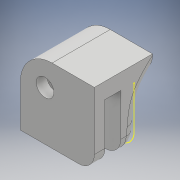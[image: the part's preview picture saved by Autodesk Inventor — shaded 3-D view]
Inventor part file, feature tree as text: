
AUTODESK INVENTOR PART (.ipt)
format: ipt  version: 2017 (Build 210142000, 142)  size: 299,520 bytes
history: native  units: mm
features: sketch x5, extrude x4, other x2, plane x1, loft x1, fillet x1, projected_geometry x1
ambient origin geometry x8: Origin, YZ Plane, XZ Plane, XY Plane, X Axis, Y Axis, Z Axis, Center Point
bodies: Solid1 (feature_tree)
feature tree (15):
  extrude  "Extrusion1"  Depth=3.0mm
  extrude  "Extrusion2"  Depth=3.0mm
  plane  "Work Plane1"
  extrude  "Extrusion3"  Depth=11.0mm TaperAngle=0.0deg
  sketch  "Sketch4"  dims[d7=2.0mm d8=0.0mm d9=3.0mm d10=2.5mm d11=0.0mm]
  loft  "Loft2"
  fillet  "Fillet1"  Radius=2.5mm
  extrude  "Extrusion4"  TaperAngle=0.0deg  [1 undecoded]
  sketch  "Sketch1"  dims[d0=3.0mm d1=3.0mm]
  sketch  "Sketch2"  dims[d2=8.0mm d3=3.0mm]
  sketch  "Sketch3"  dims[d4=8.0mm d5=11.0mm d6=0.0mm]
  projected_geometry  "Projected Loop1"
  other  "Edges3"
  other  "Edges4"
  sketch  "Sketch5"  dims[d16=0.0mm d17=90.0deg d18=0.0mm d19=90.0deg d20=2.0mm d21=3.333333mm d22=3.0mm d23=3.0mm d24=2.5mm d25=0.0mm]
note: 1 required parameter value undecoded (feature->parameter linkage not recoverable at this tier; creation-order binding heuristic only, values carry confidence <= 0.55)
